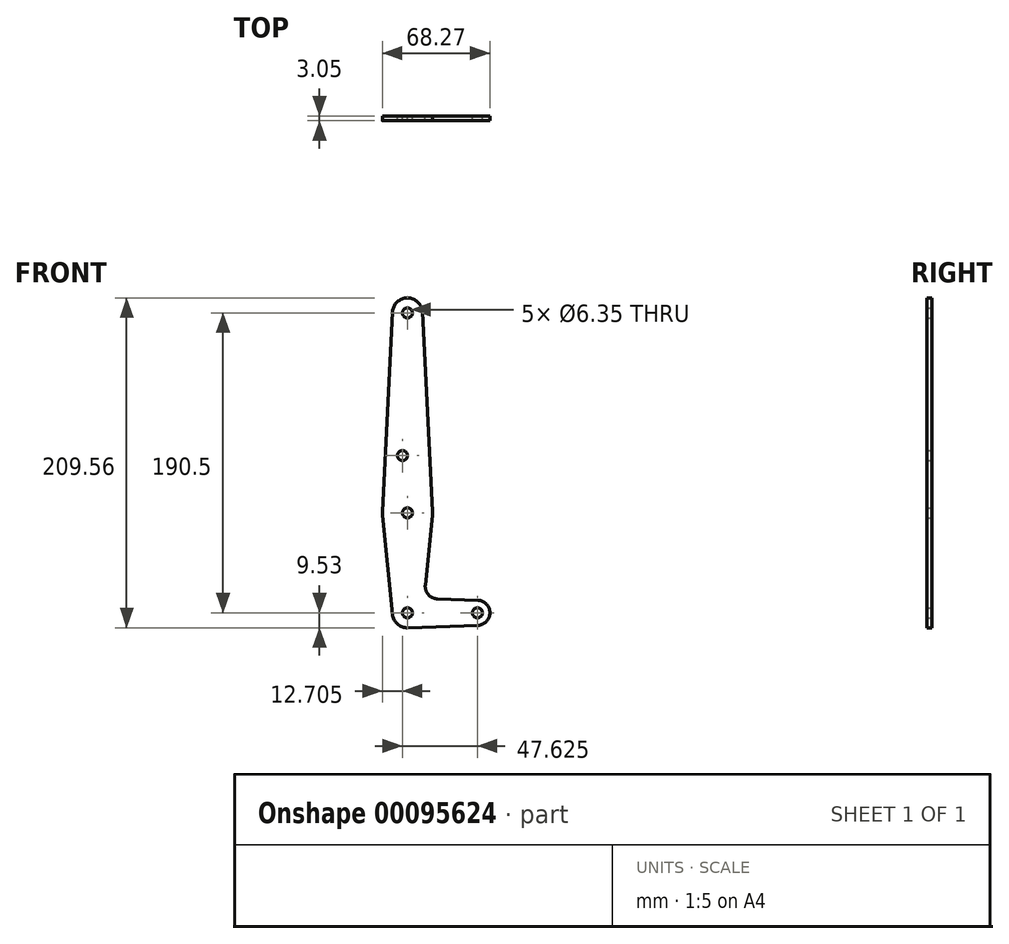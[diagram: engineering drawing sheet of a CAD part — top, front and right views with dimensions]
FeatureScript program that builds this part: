
annotation { "Feature Type Name" : "Feature", "Feature Type Description" : "" }
export const myFeature = defineFeature(function(context is Context, id is Id, definition is map)
    precondition{}
    {
        {
            var Q0;
            Q0=qCreatedBy(makeId("Front.planeOp"),FACE);
            var sketch = newSketch(context, id + "F0", { "sketchPlane" : qUnion([Q0])});
            skLineSegment(sketch, "E0", {"start": v(0, 0) * mm, "end": v(0, 127) * mm, "construction": true});
            skCircle(sketch, "E1", {"center": v(0, 0) * mm, "radius": 15.88 * mm});
            skCircle(sketch, "E2", {"center": v(0, -63.5) * mm, "radius": 9.53 * mm});
            skCircle(sketch, "E3", {"center": v(0, 127) * mm, "radius": 9.53 * mm});
            skLineSegment(sketch, "E4", {"start": v(0, 0) * mm, "end": v(0, -63.5) * mm, "construction": true});
            skLineSegment(sketch, "E5", {"start": v(0, -63.5) * mm, "end": v(44.45, -63.5) * mm, "construction": true});
            skCircle(sketch, "E6", {"center": v(44.45, -63.5) * mm, "radius": 7.94 * mm});
            skLineSegment(sketch, "E7", {"start": v(0.34, -73.02) * mm, "end": v(44.73, -71.43) * mm});
            skLineSegment(sketch, "E8", {"start": v(18.97, -54.65) * mm, "end": v(44.73, -55.57) * mm});
            skCircle(sketch, "E9", {"center": v(0, 127) * mm, "radius": 3.18 * mm});
            skCircle(sketch, "E10", {"center": v(-3.18, 36.39) * mm, "radius": 3.18 * mm});
            skCircle(sketch, "E11", {"center": v(0, 0) * mm, "radius": 3.18 * mm});
            skCircle(sketch, "E12", {"center": v(0, -63.5) * mm, "radius": 3.18 * mm});
            skCircle(sketch, "E13", {"center": v(44.45, -63.5) * mm, "radius": 3.18 * mm});
            skLineSegment(sketch, "E14", {"start": v(-9.51, 127.48) * mm, "end": v(-15.86, 0.8) * mm});
            skLineSegment(sketch, "E15", {"start": v(9.51, 127.48) * mm, "end": v(15.86, 0.8) * mm});
            skLineSegment(sketch, "E16", {"start": v(-15.8, -1.59) * mm, "end": v(-9.48, -64.45) * mm});
            skLineSegment(sketch, "E17", {"start": v(15.8, -1.59) * mm, "end": v(11.34, -45.9) * mm});
            skArc(sketch, "E18.filletArc", {"start": v(11.34, -45.9) * mm, "mid": v(13.26, -51.93) * mm, "end": v(18.97, -54.65) * mm});
            skSolve(sketch);
        }
        {
            var Q0;
            Q0 = qSketchRegion(id + "F0", true);
            extrude(context, id + "F1", {"entities" : qUnion([Q0]), "depth" : 3.05 * mm});
        }
    });
